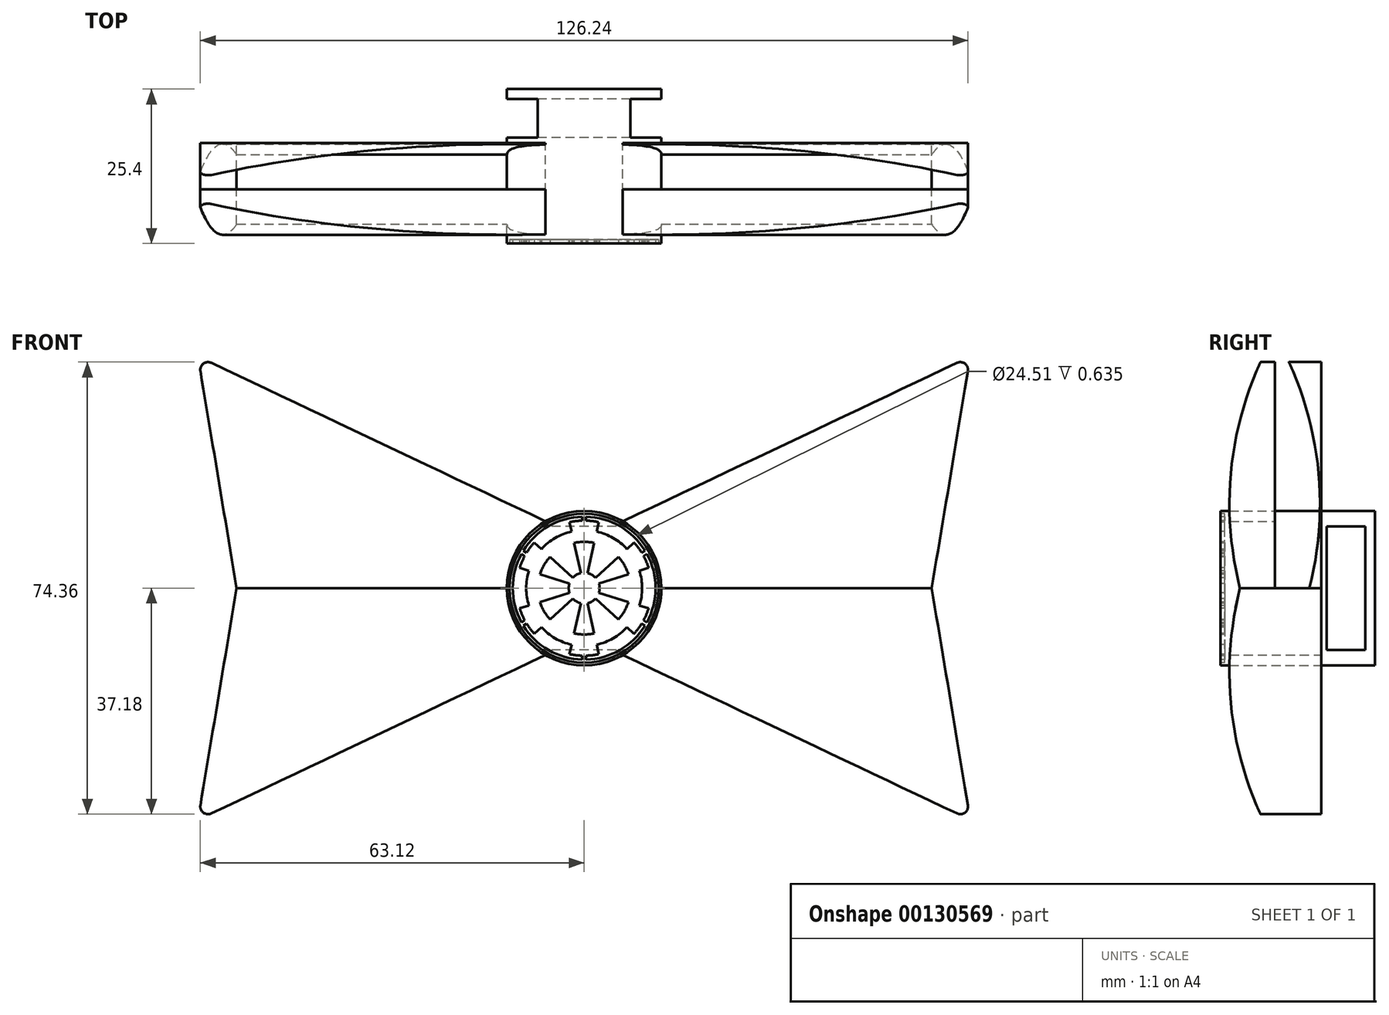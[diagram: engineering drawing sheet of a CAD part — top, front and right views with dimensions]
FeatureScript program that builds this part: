
annotation { "Feature Type Name" : "Feature", "Feature Type Description" : "" }
export const myFeature = defineFeature(function(context is Context, id is Id, definition is map)
    precondition{}
    {
        {
            var Q0;
            Q0=qCreatedBy(makeId("Front.planeOp"),FACE);
            var sketch = newSketch(context, id + "F0", { "sketchPlane" : qUnion([Q0])});
            skLineSegment(sketch, "E0", {"start": v(-61.3, 37.06) * mm, "end": v(-6.35, 11) * mm});
            skLineSegment(sketch, "E1", {"start": v(-61.3, -37.06) * mm, "end": v(-6.35, -11) * mm});
            skLineSegment(sketch, "E2", {"start": v(-63.1, 35.7) * mm, "end": v(-57.15, 0) * mm});
            skLineSegment(sketch, "E3", {"start": v(-57.15, 0) * mm, "end": v(-63.1, -35.7) * mm});
            skArc(sketch, "E4.filletArc", {"start": v(-61.3, 37.06) * mm, "mid": v(-62.61, 36.92) * mm, "end": v(-63.1, 35.7) * mm});
            skArc(sketch, "E5.filletArc", {"start": v(-63.1, -35.7) * mm, "mid": v(-62.61, -36.92) * mm, "end": v(-61.3, -37.06) * mm});
            skLineSegment(sketch, "E6.MirrorCS", {"start": v(61.3, 37.06) * mm, "end": v(6.35, 11) * mm});
            skArc(sketch, "E7.MirrorCS", {"start": v(61.3, 37.06) * mm, "mid": v(62.61, 36.92) * mm, "end": v(63.1, 35.7) * mm});
            skLineSegment(sketch, "E8.MirrorCS", {"start": v(63.1, 35.7) * mm, "end": v(57.15, 0) * mm});
            skLineSegment(sketch, "E9.MirrorCS", {"start": v(61.3, -37.06) * mm, "end": v(6.35, -11) * mm});
            skLineSegment(sketch, "E10.MirrorCS", {"start": v(57.15, 0) * mm, "end": v(63.1, -35.7) * mm});
            skArc(sketch, "E11.MirrorCS", {"start": v(63.1, -35.7) * mm, "mid": v(62.61, -36.92) * mm, "end": v(61.3, -37.06) * mm});
            skLineSegment(sketch, "E12", {"start": v(6.35, 11) * mm, "end": v(6.35, -11) * mm});
            skLineSegment(sketch, "E13", {"start": v(-6.35, 11) * mm, "end": v(-6.35, -11) * mm});
            skLineSegment(sketch, "E14", {"start": v(-6.35, 11) * mm, "end": v(6.35, 11) * mm});
            skLineSegment(sketch, "E15", {"start": v(-6.35, -11) * mm, "end": v(6.35, -11) * mm});
            skPoint(sketch, "E16", {"position": v(63.5, 0) * mm});
            skLineSegment(sketch, "E17", {"start": v(63.5, 38.1) * mm, "end": v(-63.5, 38.1) * mm});
            skPoint(sketch, "E18", {"position": v(-63.5, 0) * mm});
            skLineSegment(sketch, "E19", {"start": v(63.5, 38.1) * mm, "end": v(63.5, -38.1) * mm});
            skLineSegment(sketch, "E20", {"start": v(-63.5, 38.1) * mm, "end": v(-63.5, -38.1) * mm});
            skLineSegment(sketch, "E21", {"start": v(-63.5, -38.1) * mm, "end": v(63.5, -38.1) * mm});
            skLineSegment(sketch, "E22", {"start": v(-62.61, 36.92) * mm, "end": v(-63.5, 38.1) * mm});
            skLineSegment(sketch, "E23", {"start": v(63.5, 38.1) * mm, "end": v(62.61, 36.92) * mm});
            skLineSegment(sketch, "E24", {"start": v(63.5, -38.1) * mm, "end": v(62.61, -36.92) * mm});
            skLineSegment(sketch, "E25", {"start": v(-63.5, -38.1) * mm, "end": v(-62.61, -36.92) * mm});
            skSolve(sketch);
        }
        {
            var Q0;
            Q0=qCreatedBy(makeId("Right.planeOp"),FACE);
            cPlane(context, id + "F1", {"entities" : qUnion([Q0]), "cplaneType" : CPlaneType.OFFSET, "offset" : 63.5 * mm, "width" : 152.4 * mm, "height" : 152.4 * mm});
        }
        {
            var Q0;
            Q0=qCreatedBy(id+"F1.planeOp",FACE);
            var sketch = newSketch(context, id + "F2", { "sketchPlane" : qUnion([Q0])});
            skLineSegment(sketch, "E26.bottom", {"start": v(0, 0) * mm, "end": v(-5.71, 0) * mm});
            skLineSegment(sketch, "E26.left", {"start": v(0, 0) * mm, "end": v(0, 38.1) * mm});
            skLineSegment(sketch, "E27", {"start": v(-1.9, 38.1) * mm, "end": v(0, 38.1) * mm});
            skArc(sketch, "E28", {"start": v(-1.9, 38.1) * mm, "mid": v(-7.18, 19.39) * mm, "end": v(-5.71, 0) * mm});
            skArc(sketch, "E29.MirrorCS", {"start": v(-1.9, -38.1) * mm, "mid": v(-7.18, -19.39) * mm, "end": v(-5.71, 0) * mm});
            skLineSegment(sketch, "E30.MirrorCS", {"start": v(0, 0) * mm, "end": v(0, -38.1) * mm});
            skLineSegment(sketch, "E31.MirrorCS", {"start": v(-1.9, -38.1) * mm, "end": v(0, -38.1) * mm});
            skArc(sketch, "E32.MirrorCS", {"start": v(1.9, 38.1) * mm, "mid": v(7.18, 19.39) * mm, "end": v(5.71, 0) * mm});
            skLineSegment(sketch, "E33.MirrorCS", {"start": v(1.9, 38.1) * mm, "end": v(0, 38.1) * mm});
            skLineSegment(sketch, "E34.MirrorCS", {"start": v(0, 0) * mm, "end": v(5.71, 0) * mm});
            skArc(sketch, "E35.MirrorCS", {"start": v(1.9, -38.1) * mm, "mid": v(7.18, -19.39) * mm, "end": v(5.71, 0) * mm});
            skLineSegment(sketch, "E36.MirrorCS", {"start": v(1.9, -38.1) * mm, "end": v(0, -38.1) * mm});
            skLineSegment(sketch, "E37.bottom", {"start": v(7.87, -38.1) * mm, "end": v(-7.87, -38.1) * mm});
            skLineSegment(sketch, "E37.top", {"start": v(7.87, 38.1) * mm, "end": v(-7.87, 38.1) * mm});
            skLineSegment(sketch, "E37.left", {"start": v(7.87, -38.1) * mm, "end": v(7.87, 38.1) * mm});
            skLineSegment(sketch, "E37.right", {"start": v(-7.87, -38.1) * mm, "end": v(-7.87, 38.1) * mm});
            skPoint(sketch, "E37.middle", {"position": v(0, 0) * mm});
            skSolve(sketch);
        }
        {
            var Q0;
            {var subQ3=sQuery(id+"F0.wireOp",EDGE,"E0");Q0=makeQuery(id+"F0.imprint","IMPRINT",FACE,{"disambiguationData":[TD([[makeQuery(id+"F0.imprint","IMPRINT",EDGE,{"derivedFrom":subQ3}),-1.0]])]});}
            var Q1;
            {var subQ3=sQuery(id+"F0.wireOp",EDGE,"E6.MirrorCS");Q1=makeQuery(id+"F0.imprint","IMPRINT",FACE,{"disambiguationData":[TD([[makeQuery(id+"F0.imprint","IMPRINT",EDGE,{"derivedFrom":subQ3}),1.0]])]});}
            var Q2;
            Q2=makeQuery(id+"F0.imprint","IMPRINT",FACE,{"disambiguationData":[TD([[makeQuery(id+"F0.imprint","IMPRINT",EDGE,{"derivedFrom":sQuery(id+"F0.wireOp",EDGE,"E12")}),-1.0]])]});
            extrude(context, id + "F3", {"entities" : qUnion([Q0, Q1, Q2]), "endBound" : BoundingType.SYMMETRIC, "depth" : 15.24 * mm});
        }
        {
            var Q0;
            {var subQ1=sQuery(id+"F2.wireOp",EDGE,"E28");Q0=makeQuery(id+"F2.imprint","IMPRINT",FACE,{"disambiguationData":[TD([[makeQuery(id+"F2.imprint","IMPRINT",EDGE,{"derivedFrom":subQ1}),-1.0]])]});}
            var Q1;
            {var subQ4=sQuery(id+"F2.wireOp",EDGE,"E32.MirrorCS");Q1=makeQuery(id+"F2.imprint","IMPRINT",FACE,{"disambiguationData":[TD([[makeQuery(id+"F2.imprint","IMPRINT",EDGE,{"derivedFrom":subQ4}),1.0]])]});}
            extrude(context, id + "F4", {"entities" : qUnion([Q0, Q1]), "operationType" : NewBodyOperationType.REMOVE, "oppositeDirection" : true, "depth" : 127 * mm});
        }
        {
            var Q0;
            Q0=qCreatedBy(makeId("Front.planeOp"),FACE);
            var sketch = newSketch(context, id + "F5", { "sketchPlane" : qUnion([Q0])});
            skCircle(sketch, "E38", {"center": v(0, 0) * mm, "radius": 12.7 * mm});
            skSolve(sketch);
        }
        {
            var Q0;
            Q0=makeQuery(id+"F5.imprint","IMPRINT",FACE,{"disambiguationData":[TD([[makeQuery(id+"F5.imprint","IMPRINT",EDGE,{"derivedFrom":sQuery(id+"F5.wireOp",EDGE,"E38")}),1.0]])]});
            extrude(context, id + "F6", {"entities" : qUnion([Q0]), "operationType" : NewBodyOperationType.ADD, "endBound" : BoundingType.SYMMETRIC, "depth" : 17.78 * mm});
        }
        {
            var Q0;
            Q0=makeQuery(id+"F6.opExtrude","CAP_FACE",FACE,{"disambiguationData":[OSD([sQuery(id+"F5.wireOp",EDGE,"E38")])],"isStart":false});
            var sketch = newSketch(context, id + "F7", { "sketchPlane" : qUnion([Q0])});
            skArc(sketch, "E39", {"start": v(9.53, 0) * mm, "mid": v(9.41, 1.45) * mm, "end": v(9.08, 2.86) * mm});
            skArc(sketch, "E40", {"start": v(7.27, 2.3) * mm, "mid": v(6.6, 3.81) * mm, "end": v(5.62, 5.15) * mm});
            skArc(sketch, "E41", {"start": v(2.54, 0) * mm, "mid": v(2.51, 0.39) * mm, "end": v(2.42, 0.76) * mm});
            skLineSegment(sketch, "E42", {"start": v(-0.55, 2.48) * mm, "end": v(-1.65, 7.44) * mm});
            skLineSegment(sketch, "E43", {"start": v(0.55, 2.48) * mm, "end": v(1.65, 7.44) * mm});
            skLineSegment(sketch, "E44", {"start": v(-1.87, 1.72) * mm, "end": v(-5.62, 5.15) * mm});
            skLineSegment(sketch, "E45", {"start": v(-2.42, 0.76) * mm, "end": v(-7.27, 2.3) * mm});
            skLineSegment(sketch, "E46", {"start": v(1.87, 1.72) * mm, "end": v(5.62, 5.15) * mm});
            skLineSegment(sketch, "E47", {"start": v(2.42, 0.76) * mm, "end": v(7.27, 2.3) * mm});
            skArc(sketch, "E48.trimOffspring", {"start": v(1.87, 1.72) * mm, "mid": v(1.27, 2.2) * mm, "end": v(0.55, 2.48) * mm});
            skArc(sketch, "E49.trimOffspring", {"start": v(-0.55, 2.48) * mm, "mid": v(-1.27, 2.2) * mm, "end": v(-1.87, 1.72) * mm});
            skArc(sketch, "E50.trimOffspring", {"start": v(-2.42, 0.76) * mm, "mid": v(-2.51, 0.39) * mm, "end": v(-2.54, 0) * mm});
            skArc(sketch, "E51.MirrorCS", {"start": v(-2.42, -0.76) * mm, "mid": v(-2.51, -0.39) * mm, "end": v(-2.54, 0) * mm});
            skLineSegment(sketch, "E52.MirrorCS", {"start": v(-2.42, -0.76) * mm, "end": v(-7.27, -2.3) * mm});
            skArc(sketch, "E53.MirrorCS", {"start": v(7.27, -2.3) * mm, "mid": v(6.6, -3.81) * mm, "end": v(5.62, -5.15) * mm});
            skArc(sketch, "E54.MirrorCS", {"start": v(-0.55, -2.48) * mm, "mid": v(-1.27, -2.2) * mm, "end": v(-1.87, -1.72) * mm});
            skLineSegment(sketch, "E55.MirrorCS", {"start": v(-1.87, -1.72) * mm, "end": v(-5.62, -5.15) * mm});
            skLineSegment(sketch, "E56.MirrorCS", {"start": v(-0.55, -2.48) * mm, "end": v(-1.65, -7.44) * mm});
            skLineSegment(sketch, "E57.MirrorCS", {"start": v(0.55, -2.48) * mm, "end": v(1.65, -7.44) * mm});
            skLineSegment(sketch, "E58.MirrorCS", {"start": v(1.87, -1.72) * mm, "end": v(5.62, -5.15) * mm});
            skArc(sketch, "E59.MirrorCS", {"start": v(1.87, -1.72) * mm, "mid": v(1.27, -2.2) * mm, "end": v(0.55, -2.48) * mm});
            skArc(sketch, "E60.MirrorCS", {"start": v(2.54, 0) * mm, "mid": v(2.51, -0.39) * mm, "end": v(2.42, -0.76) * mm});
            skLineSegment(sketch, "E61.MirrorCS", {"start": v(2.42, -0.76) * mm, "end": v(7.27, -2.3) * mm});
            skArc(sketch, "E62.trimOffspring", {"start": v(-5.62, -5.15) * mm, "mid": v(-6.6, -3.8) * mm, "end": v(-7.27, -2.3) * mm});
            skArc(sketch, "E63.trimOffspring", {"start": v(1.65, -7.44) * mm, "mid": v(0, -7.62) * mm, "end": v(-1.65, -7.44) * mm});
            skArc(sketch, "E64.trimOffspring", {"start": v(1.65, 7.44) * mm, "mid": v(0, 7.62) * mm, "end": v(-1.65, 7.44) * mm});
            skArc(sketch, "E65.trimOffspring", {"start": v(-5.62, 5.15) * mm, "mid": v(-6.6, 3.8) * mm, "end": v(-7.27, 2.3) * mm});
            skLineSegment(sketch, "E66", {"start": v(-9.08, 2.86) * mm, "end": v(-10.6, 3.34) * mm});
            skLineSegment(sketch, "E67", {"start": v(-7.02, 6.43) * mm, "end": v(-8.2, 7.5) * mm});
            skLineSegment(sketch, "E68", {"start": v(-2.06, 9.3) * mm, "end": v(-2.4, 10.85) * mm});
            skLineSegment(sketch, "E69", {"start": v(2.06, 9.3) * mm, "end": v(2.4, 10.85) * mm});
            skLineSegment(sketch, "E70", {"start": v(7.02, 6.43) * mm, "end": v(8.2, 7.5) * mm});
            skLineSegment(sketch, "E71", {"start": v(9.08, 2.86) * mm, "end": v(10.6, 3.34) * mm});
            skArc(sketch, "E72.trimOffspring", {"start": v(-2.06, 9.3) * mm, "mid": v(-4.76, 8.25) * mm, "end": v(-7.02, 6.43) * mm});
            skArc(sketch, "E73.trimOffspring", {"start": v(7.02, 6.43) * mm, "mid": v(4.76, 8.25) * mm, "end": v(2.06, 9.3) * mm});
            skArc(sketch, "E74.trimOffspring", {"start": v(-9.08, 2.86) * mm, "mid": v(-9.41, 1.45) * mm, "end": v(-9.53, 0) * mm});
            skLineSegment(sketch, "E75", {"start": v(0.32, 11.74) * mm, "end": v(0.32, 11.1) * mm});
            skLineSegment(sketch, "E76", {"start": v(-0.32, 11.74) * mm, "end": v(-0.32, 11.1) * mm});
            skArc(sketch, "E77.trimOffspring", {"start": v(-0.32, 11.1) * mm, "mid": v(-1.37, 11.03) * mm, "end": v(-2.4, 10.85) * mm});
            skArc(sketch, "E78.trimOffspring", {"start": v(-0.32, 11.74) * mm, "mid": v(-5.86, 10.18) * mm, "end": v(-10, 6.18) * mm});
            skLineSegment(sketch, "E79", {"start": v(-9.46, 5.83) * mm, "end": v(-10, 6.18) * mm});
            skLineSegment(sketch, "E80", {"start": v(-9.78, 5.28) * mm, "end": v(-10.31, 5.63) * mm});
            skArc(sketch, "E81.trimOffspring", {"start": v(-9.78, 5.28) * mm, "mid": v(-10.23, 4.33) * mm, "end": v(-10.6, 3.34) * mm});
            skArc(sketch, "E82.trimOffspring", {"start": v(-10.31, 5.63) * mm, "mid": v(-11.38, 2.9) * mm, "end": v(-11.75, 0) * mm});
            skLineSegment(sketch, "E83.MirrorCS", {"start": v(9.46, 5.83) * mm, "end": v(10, 6.18) * mm});
            skArc(sketch, "E84.MirrorCS", {"start": v(0.32, 11.1) * mm, "mid": v(1.37, 11.03) * mm, "end": v(2.4, 10.85) * mm});
            skLineSegment(sketch, "E85.MirrorCS", {"start": v(9.78, 5.28) * mm, "end": v(10.31, 5.63) * mm});
            skArc(sketch, "E86.trimOffspring", {"start": v(-8.2, 7.5) * mm, "mid": v(-8.87, 6.7) * mm, "end": v(-9.46, 5.83) * mm});
            skArc(sketch, "E87.trimOffspring", {"start": v(8.2, 7.5) * mm, "mid": v(8.87, 6.7) * mm, "end": v(9.46, 5.83) * mm});
            skArc(sketch, "E88.MirrorCS", {"start": v(9.78, 5.28) * mm, "mid": v(10.23, 4.33) * mm, "end": v(10.6, 3.34) * mm});
            skArc(sketch, "E89.MirrorCS", {"start": v(10.31, 5.63) * mm, "mid": v(11.38, 2.9) * mm, "end": v(11.75, 0) * mm});
            skArc(sketch, "E90.MirrorCS", {"start": v(-9.08, -2.86) * mm, "mid": v(-9.41, -1.45) * mm, "end": v(-9.53, 0) * mm});
            skArc(sketch, "E91.MirrorCS", {"start": v(-10.31, -5.63) * mm, "mid": v(-11.38, -2.9) * mm, "end": v(-11.75, 0) * mm});
            skLineSegment(sketch, "E92.MirrorCS", {"start": v(-9.08, -2.86) * mm, "end": v(-10.6, -3.34) * mm});
            skArc(sketch, "E93.MirrorCS", {"start": v(-9.78, -5.28) * mm, "mid": v(-10.23, -4.33) * mm, "end": v(-10.6, -3.34) * mm});
            skLineSegment(sketch, "E94.MirrorCS", {"start": v(-9.78, -5.28) * mm, "end": v(-10.31, -5.63) * mm});
            skArc(sketch, "E95.MirrorCS", {"start": v(9.53, 0) * mm, "mid": v(9.41, -1.45) * mm, "end": v(9.08, -2.86) * mm});
            skLineSegment(sketch, "E96.MirrorCS", {"start": v(9.08, -2.86) * mm, "end": v(10.6, -3.34) * mm});
            skArc(sketch, "E97.MirrorCS", {"start": v(9.78, -5.28) * mm, "mid": v(10.23, -4.33) * mm, "end": v(10.6, -3.34) * mm});
            skLineSegment(sketch, "E98.MirrorCS", {"start": v(9.78, -5.28) * mm, "end": v(10.31, -5.63) * mm});
            skArc(sketch, "E99.MirrorCS", {"start": v(10.31, -5.63) * mm, "mid": v(11.38, -2.9) * mm, "end": v(11.75, 0) * mm});
            skArc(sketch, "E100.MirrorCS", {"start": v(-2.06, -9.3) * mm, "mid": v(-4.76, -8.25) * mm, "end": v(-7.02, -6.43) * mm});
            skLineSegment(sketch, "E101.MirrorCS", {"start": v(-7.02, -6.43) * mm, "end": v(-8.2, -7.5) * mm});
            skArc(sketch, "E102.MirrorCS", {"start": v(-8.2, -7.5) * mm, "mid": v(-8.87, -6.7) * mm, "end": v(-9.46, -5.83) * mm});
            skLineSegment(sketch, "E103.MirrorCS", {"start": v(-9.46, -5.83) * mm, "end": v(-10, -6.18) * mm});
            skArc(sketch, "E104.MirrorCS", {"start": v(-0.32, -11.74) * mm, "mid": v(-5.86, -10.18) * mm, "end": v(-10, -6.18) * mm});
            skLineSegment(sketch, "E105.MirrorCS", {"start": v(-0.32, -11.74) * mm, "end": v(-0.32, -11.1) * mm});
            skArc(sketch, "E106.MirrorCS", {"start": v(-0.32, -11.1) * mm, "mid": v(-1.37, -11.03) * mm, "end": v(-2.4, -10.85) * mm});
            skLineSegment(sketch, "E107.MirrorCS", {"start": v(-2.06, -9.3) * mm, "end": v(-2.4, -10.85) * mm});
            skLineSegment(sketch, "E108.MirrorCS", {"start": v(2.06, -9.3) * mm, "end": v(2.4, -10.85) * mm});
            skArc(sketch, "E109.MirrorCS", {"start": v(0.32, -11.1) * mm, "mid": v(1.37, -11.03) * mm, "end": v(2.4, -10.85) * mm});
            skLineSegment(sketch, "E110.MirrorCS", {"start": v(0.32, -11.74) * mm, "end": v(0.32, -11.1) * mm});
            skArc(sketch, "E111.MirrorCS", {"start": v(0.32, -11.74) * mm, "mid": v(5.86, -10.18) * mm, "end": v(10, -6.18) * mm});
            skArc(sketch, "E112.MirrorCS", {"start": v(8.2, -7.5) * mm, "mid": v(8.87, -6.7) * mm, "end": v(9.46, -5.83) * mm});
            skArc(sketch, "E113.MirrorCS", {"start": v(7.02, -6.43) * mm, "mid": v(4.76, -8.25) * mm, "end": v(2.06, -9.3) * mm});
            skLineSegment(sketch, "E114.MirrorCS", {"start": v(9.46, -5.83) * mm, "end": v(10, -6.18) * mm});
            skLineSegment(sketch, "E115.MirrorCS", {"start": v(7.02, -6.43) * mm, "end": v(8.2, -7.5) * mm});
            skArc(sketch, "E116.MirrorCS", {"start": v(0.32, 11.74) * mm, "mid": v(5.86, 10.18) * mm, "end": v(10, 6.18) * mm});
            skCircle(sketch, "E117", {"center": v(0, 0) * mm, "radius": 12.26 * mm});
            skSolve(sketch);
        }
        {
            var Q0;
            Q0 = qSketchRegion(id + "F7", true);
            extrude(context, id + "F8", {"entities" : qUnion([Q0]), "operationType" : NewBodyOperationType.REMOVE, "oppositeDirection" : true, "depth" : 0.64 * mm});
        }
        {
            var Q0;
            Q0=makeQuery(id+"F6.opExtrude","CAP_FACE",FACE,{"disambiguationData":[OSD([sQuery(id+"F5.wireOp",EDGE,"E38")])],"isStart":true});
            var sketch = newSketch(context, id + "F9", { "sketchPlane" : qUnion([Q0])});
            skCircle(sketch, "E118", {"center": v(0, 0) * mm, "radius": 12.7 * mm});
            skSolve(sketch);
        }
        {
            var Q0;
            Q0=makeQuery(id+"F9.imprint","IMPRINT",FACE,{"disambiguationData":[TD([[makeQuery(id+"F9.imprint","IMPRINT",EDGE,{"derivedFrom":sQuery(id+"F9.wireOp",EDGE,"E118")}),-1.0]])]});
            extrude(context, id + "F10", {"entities" : qUnion([Q0]), "operationType" : NewBodyOperationType.ADD, "depth" : 7.62 * mm});
        }
        {
            var Q0;
            Q0=qCreatedBy(makeId("Right.planeOp"),FACE);
            var sketch = newSketch(context, id + "F11", { "sketchPlane" : qUnion([Q0])});
            skPoint(sketch, "E119.middle", {"position": v(0, 0) * mm});
            skLineSegment(sketch, "E120.bottom", {"start": v(14.86, -10.16) * mm, "end": v(8.5, -10.16) * mm});
            skLineSegment(sketch, "E120.top", {"start": v(14.86, 10.16) * mm, "end": v(8.5, 10.16) * mm});
            skLineSegment(sketch, "E120.left", {"start": v(14.86, -10.16) * mm, "end": v(14.86, 10.16) * mm});
            skLineSegment(sketch, "E120.right", {"start": v(8.5, -10.16) * mm, "end": v(8.5, 10.16) * mm});
            skPoint(sketch, "E120.middle", {"position": v(11.68, 0) * mm});
            skSolve(sketch);
        }
        {
            var Q0;
            Q0 = qSketchRegion(id + "F11", true);
            extrude(context, id + "F12", {"entities" : qUnion([Q0]), "operationType" : NewBodyOperationType.REMOVE, "endBound" : BoundingType.SYMMETRIC, "depth" : 50.8 * mm});
        }
    });
